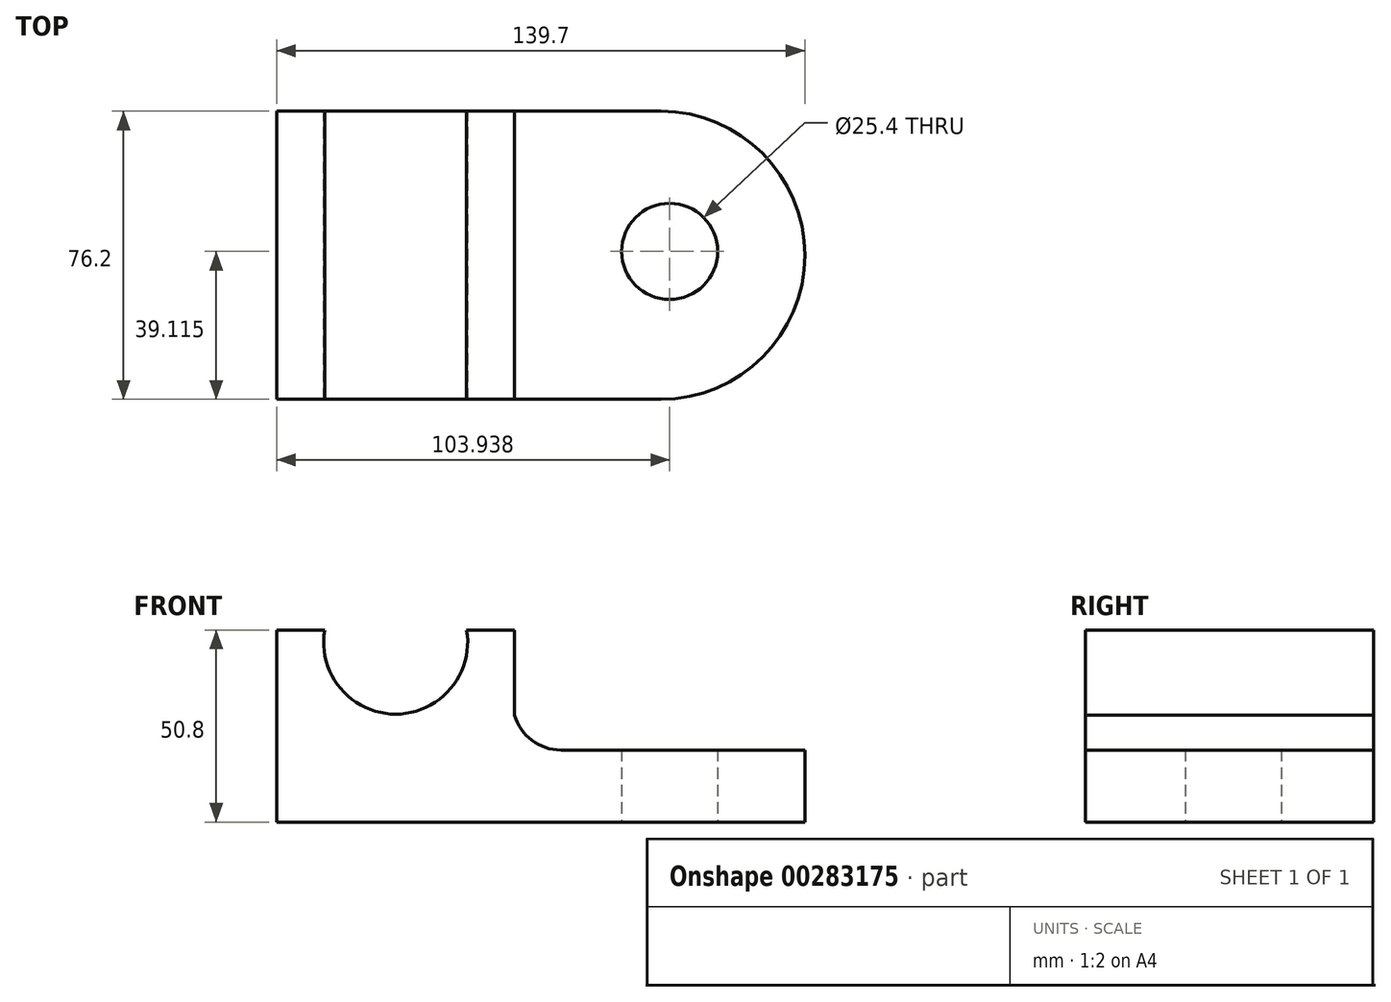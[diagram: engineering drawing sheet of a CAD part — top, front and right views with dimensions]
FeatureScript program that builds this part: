
annotation { "Feature Type Name" : "Feature", "Feature Type Description" : "" }
export const myFeature = defineFeature(function(context is Context, id is Id, definition is map)
    precondition{}
    {
        {
            var Q0;
            Q0=qCreatedBy(makeId("Front.planeOp"),FACE);
            var sketch = newSketch(context, id + "F0", { "sketchPlane" : qUnion([Q0])});
            skLineSegment(sketch, "E0", {"start": v(-62.95, 33.02) * mm, "end": v(-62.95, -17.78) * mm});
            skLineSegment(sketch, "E1", {"start": v(-62.95, 33.02) * mm, "end": v(-50.25, 33.02) * mm});
            skLineSegment(sketch, "E2", {"start": v(-62.95, -17.78) * mm, "end": v(76.75, -17.78) * mm});
            skLineSegment(sketch, "E3", {"start": v(76.75, -17.78) * mm, "end": v(76.75, 1.27) * mm});
            skLineSegment(sketch, "E4", {"start": v(76.75, 1.27) * mm, "end": v(12.22, 1.27) * mm});
            skArc(sketch, "E5", {"start": v(12.22, 1.27) * mm, "mid": v(4.56, 3.85) * mm, "end": v(0, 10.53) * mm});
            skLineSegment(sketch, "E6", {"start": v(0, 10.53) * mm, "end": v(0, 33.02) * mm});
            skLineSegment(sketch, "E7", {"start": v(0, 33.02) * mm, "end": v(-12.7, 33.02) * mm});
            skArc(sketch, "E8", {"start": v(-50.25, 33.02) * mm, "mid": v(-31.48, 10.76) * mm, "end": v(-12.7, 33.02) * mm});
            skSolve(sketch);
        }
        {
            var Q0;
            Q0 = qSketchRegion(id + "F0", true);
            extrude(context, id + "F1", {"entities" : qUnion([Q0]), "depth" : 76.2 * mm});
        }
        {
            var Q0;
            Q0=makeQuery(id+"F1.opExtrude","CAP_EDGE",EDGE,{"disambiguationData":[OSD([sQuery(id+"F0.wireOp",EDGE,"E3")])],"isStart":false});
            var Q1;
            Q1=makeQuery(id+"F1.opExtrude","CAP_EDGE",EDGE,{"disambiguationData":[OSD([sQuery(id+"F0.wireOp",EDGE,"E3")])],"isStart":true});
            fillet(context, id + "F2", {"entities" : qUnion([Q0, Q1]), "radius" : 38.1 * mm, "tangentPropagation" : true, "allowEdgeOverflow" : false});
        }
        {
            var Q0;
            Q0=qCreatedBy(makeId("Top.planeOp"),FACE);
            var sketch = newSketch(context, id + "F3", { "sketchPlane" : qUnion([Q0])});
            skCircle(sketch, "E9", {"center": v(40.99, -37.08) * mm, "radius": 12.7 * mm});
            skSolve(sketch);
        }
        {
            var Q0;
            Q0 = qSketchRegion(id + "F3", true);
            extrude(context, id + "F4", {"entities" : qUnion([Q0]), "operationType" : NewBodyOperationType.REMOVE, "depth" : 50.8 * mm});
        }
        {
            var Q0;
            Q0=makeQuery(id+"F4.boolean.opBoolean","COPY",FACE,{"derivedFrom":makeQuery(id+"F4.opExtrude","CAP_FACE",FACE,{"disambiguationData":[OSD([sQuery(id+"F3.wireOp",EDGE,"E9")])],"isStart":true})});
            extrude(context, id + "F5", {"entities" : qUnion([Q0]), "operationType" : NewBodyOperationType.REMOVE, "oppositeDirection" : true, "depth" : 25.4 * mm});
        }
    });
